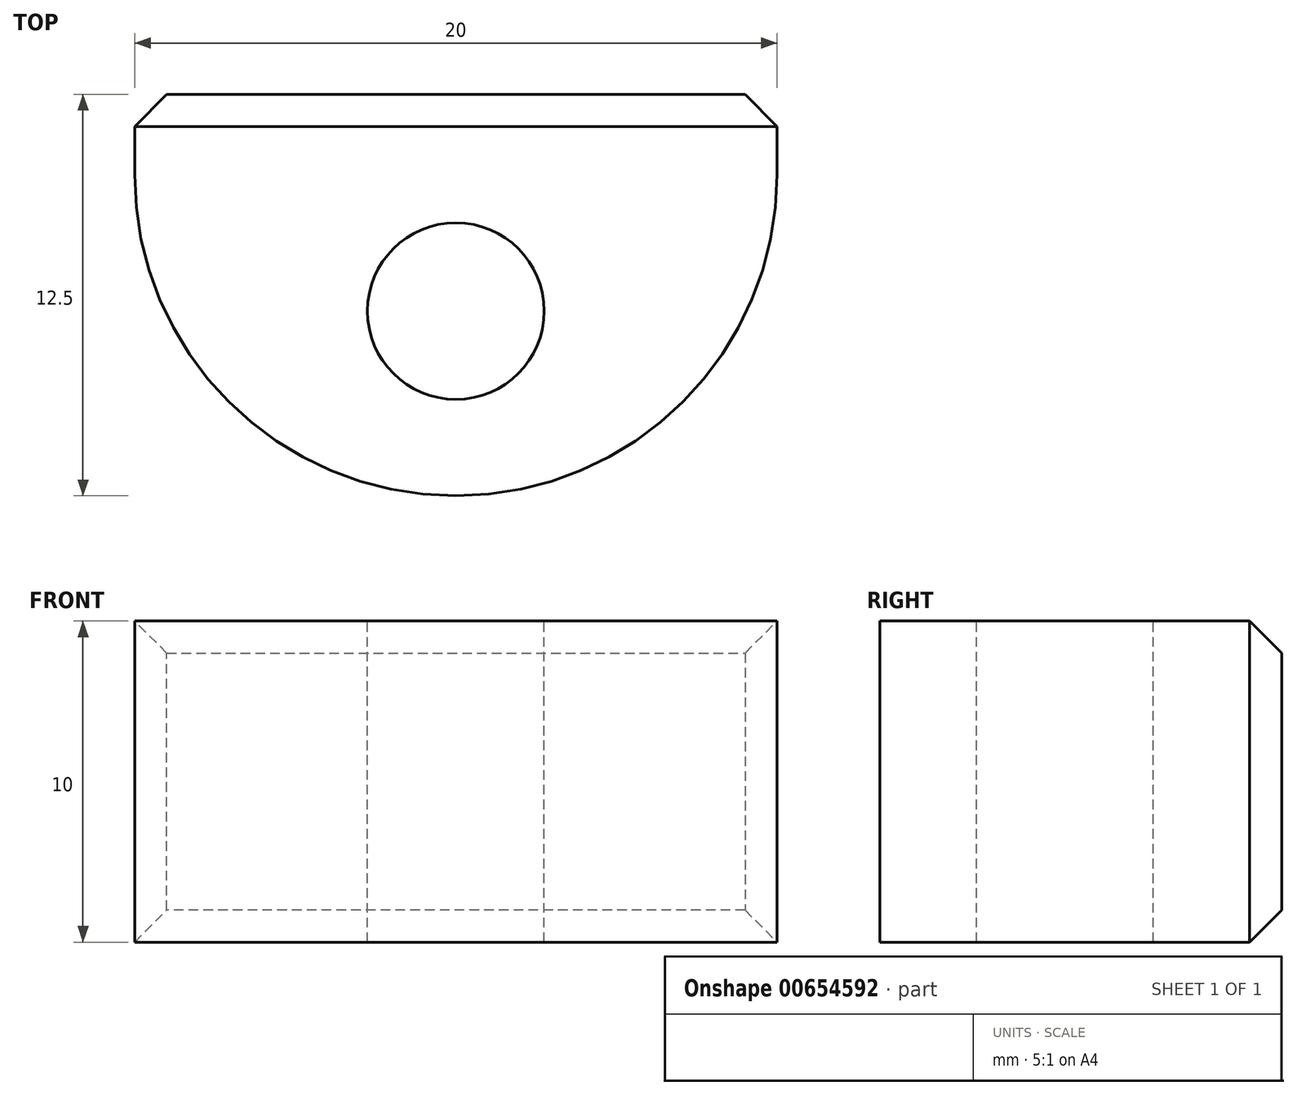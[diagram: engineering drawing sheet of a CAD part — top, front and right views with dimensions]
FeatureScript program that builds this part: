
annotation { "Feature Type Name" : "Feature", "Feature Type Description" : "" }
export const myFeature = defineFeature(function(context is Context, id is Id, definition is map)
    precondition{}
    {
        {
            var Q0;
            Q0=qCreatedBy(makeId("Front.planeOp"),FACE);
            var sketch = newSketch(context, id + "F0", { "sketchPlane" : qUnion([Q0])});
            skLineSegment(sketch, "E0.bottom", {"start": v(0, 0) * mm, "end": v(20, 0) * mm});
            skLineSegment(sketch, "E0.top", {"start": v(0, 10) * mm, "end": v(20, 10) * mm});
            skLineSegment(sketch, "E0.left", {"start": v(0, 0) * mm, "end": v(0, 10) * mm});
            skLineSegment(sketch, "E0.right", {"start": v(20, 0) * mm, "end": v(20, 10) * mm});
            skSolve(sketch);
        }
        {
            var Q0;
            Q0=makeQuery(id+"F0.imprint","IMPRINT",FACE,{"disambiguationData":[TD([[makeQuery(id+"F0.imprint","IMPRINT",EDGE,{"derivedFrom":sQuery(id+"F0.wireOp",EDGE,"E0.bottom")}),1.0]])]});
            extrude(context, id + "F1", {"entities" : qUnion([Q0]), "depth" : 12.5 * mm, "offsetDistance" : 25 * mm});
        }
        {
            var Q0;
            Q0=makeQuery(id+"F1.opExtrude","SWEPT_FACE",FACE,{"disambiguationData":[OSD([sQuery(id+"F0.wireOp",EDGE,"E0.top")])]});
            var sketch = newSketch(context, id + "F2", { "sketchPlane" : qUnion([Q0])});
            skCircle(sketch, "E1", {"center": v(10, -6.75) * mm, "radius": 2.75 * mm});
            skSolve(sketch);
        }
        {
            var Q0;
            Q0=makeQuery(id+"F2.imprint","IMPRINT",FACE,{"disambiguationData":[TD([[makeQuery(id+"F2.imprint","IMPRINT",EDGE,{"derivedFrom":sQuery(id+"F2.wireOp",EDGE,"E1")}),1.0]])]});
            extrude(context, id + "F3", {"entities" : qUnion([Q0]), "operationType" : NewBodyOperationType.REMOVE, "endBound" : BoundingType.UP_TO_NEXT, "oppositeDirection" : true, "depth" : 25 * mm, "offsetDistance" : 25 * mm});
        }
        {
            var Q0;
            Q0=makeQuery(id+"F1.opExtrude","CAP_EDGE",EDGE,{"disambiguationData":[OSD([sQuery(id+"F0.wireOp",EDGE,"E0.left")])],"isStart":false});
            var Q1;
            Q1=makeQuery(id+"F1.opExtrude","CAP_EDGE",EDGE,{"disambiguationData":[OSD([sQuery(id+"F0.wireOp",EDGE,"E0.right")])],"isStart":false});
            fillet(context, id + "F4", {"entities" : qUnion([Q0, Q1]), "radius" : 10 * mm, "tangentPropagation" : true, "allowEdgeOverflow" : false});
        }
        {
            var Q0;
            Q0=makeQuery(id+"F4.opFillet","BLEND_FACE",FACE,{"disambiguationData":[OSD([sQuery(id+"F0.wireOp",EDGE,"E0.right")])]});
            var Q1;
            Q1=makeQuery(id+"F1.opExtrude","CAP_FACE",FACE,{"disambiguationData":[OSD([sQuery(id+"F0.wireOp",EDGE,"E0.bottom"),sQuery(id+"F0.wireOp",EDGE,"E0.top"),sQuery(id+"F0.wireOp",EDGE,"E0.left"),sQuery(id+"F0.wireOp",EDGE,"E0.right")])],"isStart":true});
            chamfer(context, id + "F5", {"entities" : qUnion([Q0, Q1]), "width" : 1 * mm, "tangentPropagation" : true});
        }
    });
